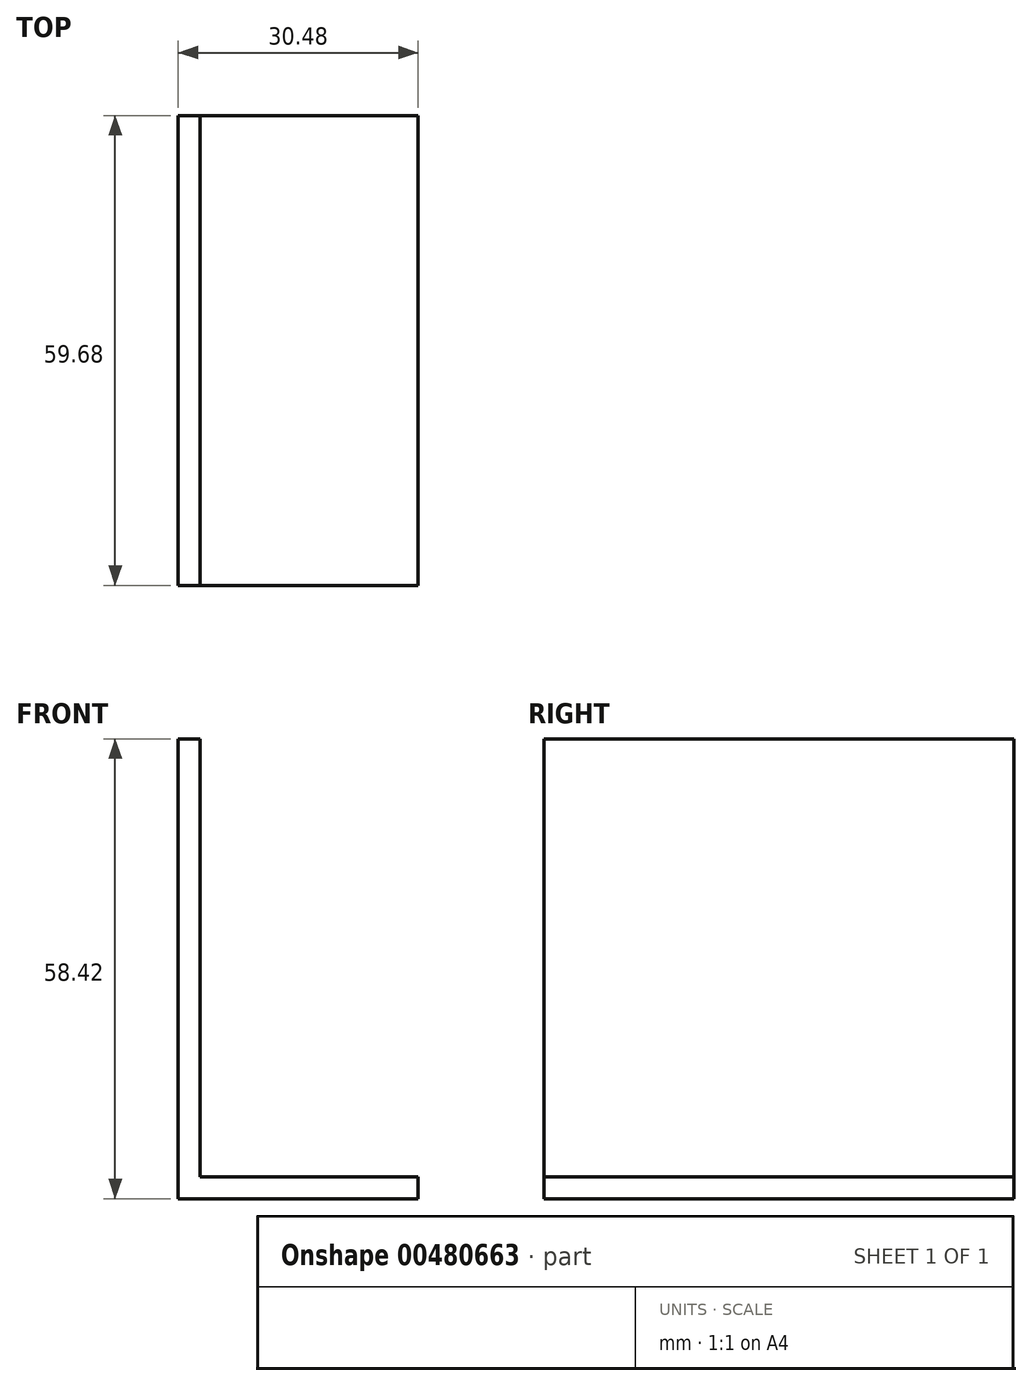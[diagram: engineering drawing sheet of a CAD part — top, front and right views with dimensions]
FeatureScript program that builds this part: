
annotation { "Feature Type Name" : "Feature", "Feature Type Description" : "" }
export const myFeature = defineFeature(function(context is Context, id is Id, definition is map)
    precondition{}
    {
        {
            var Q0;
            Q0=qCreatedBy(makeId("Front.planeOp"),FACE);
            var sketch = newSketch(context, id + "F0", { "sketchPlane" : qUnion([Q0])});
            skLineSegment(sketch, "E0", {"start": v(-24.89, 12.97) * mm, "end": v(-55.37, 12.97) * mm});
            skLineSegment(sketch, "E1", {"start": v(-55.37, 12.97) * mm, "end": v(-55.37, 71.4) * mm});
            skLineSegment(sketch, "E2.0", {"start": v(-52.57, 12.97) * mm, "end": v(-52.57, 71.4) * mm});
            skLineSegment(sketch, "E3.0", {"start": v(-24.89, 15.77) * mm, "end": v(-55.37, 15.77) * mm});
            skLineSegment(sketch, "E4", {"start": v(-24.89, 12.97) * mm, "end": v(-24.89, 15.77) * mm});
            skLineSegment(sketch, "E5", {"start": v(-52.57, 71.4) * mm, "end": v(-55.37, 71.4) * mm});
            skSolve(sketch);
        }
        {
            var Q0;
            Q0 = qSketchRegion(id + "F0", true);
            extrude(context, id + "F1", {"entities" : qUnion([Q0]), "endBound" : BoundingType.SYMMETRIC, "depth" : 59.69 * mm});
        }
    });
